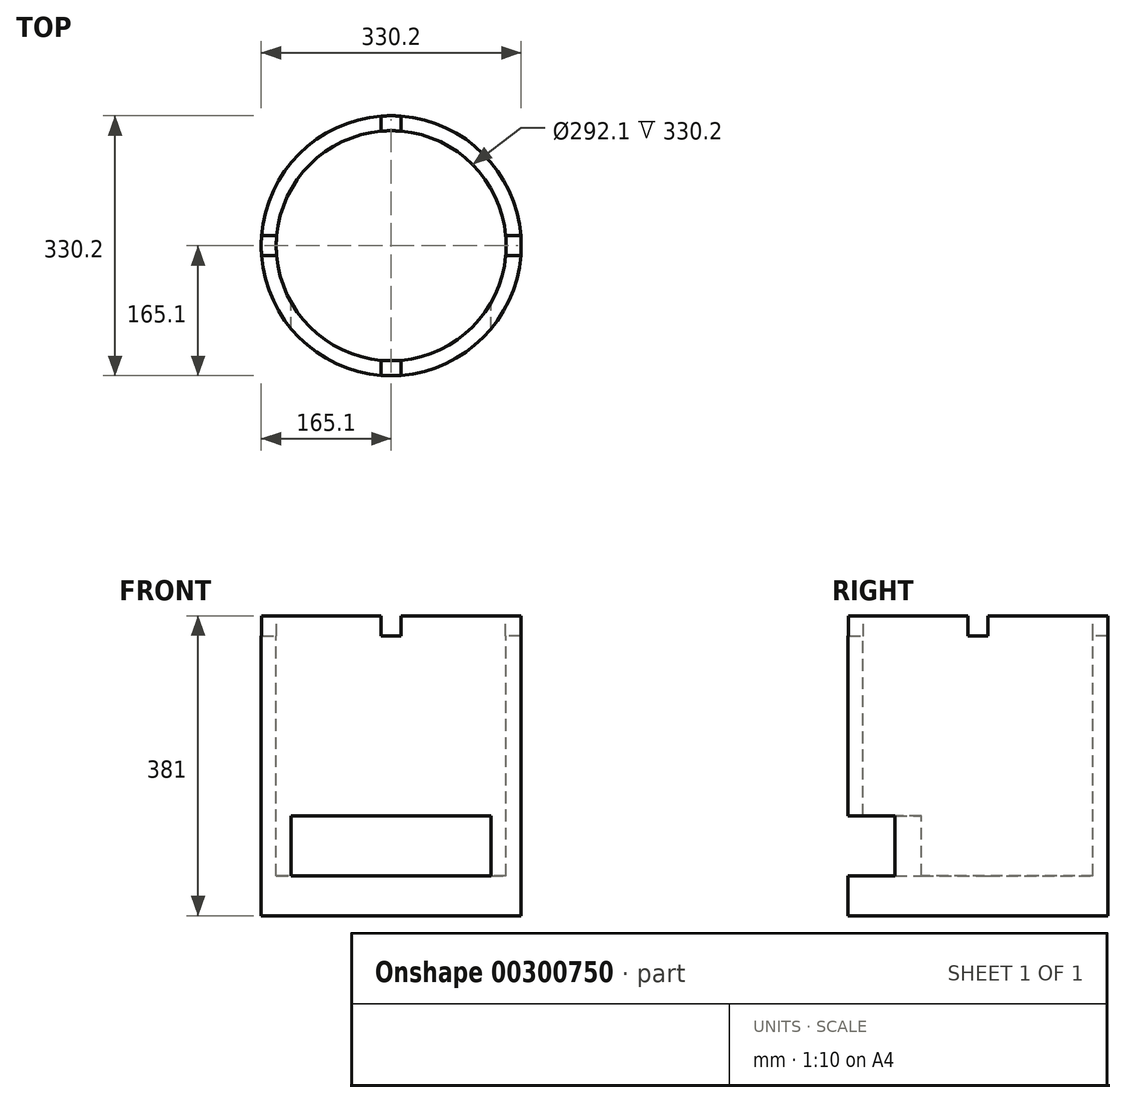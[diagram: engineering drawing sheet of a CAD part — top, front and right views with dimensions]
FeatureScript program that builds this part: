
annotation { "Feature Type Name" : "Feature", "Feature Type Description" : "" }
export const myFeature = defineFeature(function(context is Context, id is Id, definition is map)
    precondition{}
    {
        {
            var Q0;
            Q0=qCreatedBy(makeId("Top.planeOp"),FACE);
            var sketch = newSketch(context, id + "F0", { "sketchPlane" : qUnion([Q0])});
            skCircle(sketch, "E0", {"center": v(0, 0) * mm, "radius": 165.1 * mm});
            skSolve(sketch);
        }
        {
            var Q0;
            Q0=makeQuery(id+"F0.imprint","IMPRINT",FACE,{"disambiguationData":[TD([[makeQuery(id+"F0.imprint","IMPRINT",EDGE,{"derivedFrom":sQuery(id+"F0.wireOp",EDGE,"E0")}),1.0]])]});
            extrude(context, id + "F1", {"entities" : qUnion([Q0]), "depth" : 381 * mm});
        }
        {
            var Q0;
            Q0=makeQuery(id+"F1.opExtrude","CAP_FACE",FACE,{"disambiguationData":[OSD([sQuery(id+"F0.wireOp",EDGE,"E0")])],"isStart":false});
            var sketch = newSketch(context, id + "F2", { "sketchPlane" : qUnion([Q0])});
            skPoint(sketch, "E1.0", {"position": v(0, 0) * mm});
            skCircle(sketch, "E2", {"center": v(0, 0) * mm, "radius": 146.05 * mm});
            skSolve(sketch);
        }
        {
            var Q0;
            Q0=makeQuery(id+"F2.imprint","IMPRINT",FACE,{"disambiguationData":[TD([[makeQuery(id+"F2.imprint","IMPRINT",EDGE,{"derivedFrom":sQuery(id+"F2.wireOp",EDGE,"E2")}),1.0]])]});
            extrude(context, id + "F3", {"entities" : qUnion([Q0]), "operationType" : NewBodyOperationType.REMOVE, "oppositeDirection" : true, "depth" : 330.2 * mm});
        }
        {
            var Q0;
            Q0=qCreatedBy(makeId("Front.planeOp"),FACE);
            var sketch = newSketch(context, id + "F4", { "sketchPlane" : qUnion([Q0])});
            skLineSegment(sketch, "E3", {"start": v(-165.1, 0) * mm, "end": v(-165.1, 381) * mm});
            skLineSegment(sketch, "E4", {"start": v(165.1, 381) * mm, "end": v(165.1, 0) * mm});
            skLineSegment(sketch, "E5", {"start": v(165.1, 381) * mm, "end": v(-165.1, 381) * mm});
            skLineSegment(sketch, "E6", {"start": v(165.1, 0) * mm, "end": v(-165.1, 0) * mm});
            skPoint(sketch, "E7", {"position": v(0, 0) * mm});
            skLineSegment(sketch, "E8", {"start": v(0, 381) * mm, "end": v(0, 0) * mm, "construction": true});
            skLineSegment(sketch, "E9.bottom", {"start": v(127, 127) * mm, "end": v(-127, 127) * mm});
            skLineSegment(sketch, "E9.top", {"start": v(127, 50.8) * mm, "end": v(-127, 50.8) * mm});
            skLineSegment(sketch, "E9.left", {"start": v(127, 127) * mm, "end": v(127, 50.8) * mm});
            skLineSegment(sketch, "E9.right", {"start": v(-127, 127) * mm, "end": v(-127, 50.8) * mm});
            skPoint(sketch, "E10", {"position": v(-514.73, 96.28) * mm});
            skSolve(sketch);
        }
        {
            var Q0;
            Q0=makeQuery(id+"F4.imprint","IMPRINT",FACE,{"disambiguationData":[TD([[makeQuery(id+"F4.imprint","IMPRINT",EDGE,{"derivedFrom":sQuery(id+"F4.wireOp",EDGE,"E9.bottom")}),1.0]])]});
            extrude(context, id + "F5", {"entities" : qUnion([Q0]), "operationType" : NewBodyOperationType.REMOVE, "depth" : 177.8 * mm});
        }
        {
            var Q0;
            Q0=makeQuery(id+"F1.opExtrude","CAP_FACE",FACE,{"disambiguationData":[OSD([sQuery(id+"F0.wireOp",EDGE,"E0")])],"isStart":false});
            var sketch = newSketch(context, id + "F6", { "sketchPlane" : qUnion([Q0])});
            skCircle(sketch, "E11.0.0", {"center": v(0, 0) * mm, "radius": 165.1 * mm, "construction": true});
            skCircle(sketch, "E12.0", {"center": v(0, 0) * mm, "radius": 146.05 * mm, "construction": true});
            skLineSegment(sketch, "E13", {"start": v(-165.1, 0) * mm, "end": v(165.1, 0) * mm, "construction": true});
            skLineSegment(sketch, "E14", {"start": v(0, 165.1) * mm, "end": v(0, -165.1) * mm, "construction": true});
            skLineSegment(sketch, "E15.bottom", {"start": v(-12.7, 165.1) * mm, "end": v(12.7, 165.1) * mm});
            skLineSegment(sketch, "E15.top", {"start": v(-12.7, 145.5) * mm, "end": v(12.7, 145.5) * mm});
            skLineSegment(sketch, "E15.left", {"start": v(-12.7, 165.1) * mm, "end": v(-12.7, 145.5) * mm});
            skLineSegment(sketch, "E15.right", {"start": v(12.7, 165.1) * mm, "end": v(12.7, 145.5) * mm});
            skLineSegment(sketch, "E16.bottom", {"start": v(-165.1, -12.7) * mm, "end": v(-145.5, -12.7) * mm});
            skLineSegment(sketch, "E16.top", {"start": v(-165.1, 12.7) * mm, "end": v(-145.5, 12.7) * mm});
            skLineSegment(sketch, "E16.left", {"start": v(-165.1, -12.7) * mm, "end": v(-165.1, 12.7) * mm});
            skLineSegment(sketch, "E16.right", {"start": v(-145.5, -12.7) * mm, "end": v(-145.5, 12.7) * mm});
            skLineSegment(sketch, "E17.bottom", {"start": v(165.1, 12.7) * mm, "end": v(145.5, 12.7) * mm});
            skLineSegment(sketch, "E17.top", {"start": v(165.1, -12.7) * mm, "end": v(145.5, -12.7) * mm});
            skLineSegment(sketch, "E17.left", {"start": v(165.1, 12.7) * mm, "end": v(165.1, -12.7) * mm});
            skLineSegment(sketch, "E17.right", {"start": v(145.5, 12.7) * mm, "end": v(145.5, -12.7) * mm});
            skLineSegment(sketch, "E18.bottom", {"start": v(12.7, -165.1) * mm, "end": v(-12.7, -165.1) * mm});
            skLineSegment(sketch, "E18.top", {"start": v(12.7, -145.5) * mm, "end": v(-12.7, -145.5) * mm});
            skLineSegment(sketch, "E18.left", {"start": v(12.7, -165.1) * mm, "end": v(12.7, -145.5) * mm});
            skLineSegment(sketch, "E18.right", {"start": v(-12.7, -165.1) * mm, "end": v(-12.7, -145.5) * mm});
            skSolve(sketch);
        }
        {
            var Q0;
            {var subQ0=makeQuery(id+"F1.opExtrude","CAP_EDGE",EDGE,{"disambiguationData":[OSD([sQuery(id+"F0.wireOp",EDGE,"E0")])],"isStart":false});var subQ1=makeQuery(id+"F6.imprint","INTERSECT",VERTEX,{"derivedFrom":[subQ0,sQuery(id+"F6.wireOp",EDGE,"E15.bottom")]});Q0=makeQuery(id+"F6.imprint","IMPRINT",FACE,{"disambiguationData":[TD([[makeQuery(id+"F6.imprint","IMPRINT",EDGE,{"disambiguationData":[TD([[subQ1,-1.0]])],"derivedFrom":subQ0}),1.0]])]});}
            var Q1;
            {var subQ0=sQuery(id+"F6.wireOp",EDGE,"E16.bottom");var subQ1=makeQuery(id+"F1.opExtrude","CAP_EDGE",EDGE,{"disambiguationData":[OSD([sQuery(id+"F0.wireOp",EDGE,"E0")])],"isStart":false});var subQ2=makeQuery(id+"F6.imprint","INTERSECT",VERTEX,{"derivedFrom":[subQ1,subQ0]});Q1=makeQuery(id+"F6.imprint","IMPRINT",FACE,{"disambiguationData":[TD([[makeQuery(id+"F6.imprint","IMPRINT",EDGE,{"disambiguationData":[TD([[subQ2,1.0]])],"derivedFrom":subQ1}),1.0]])]});}
            var Q2;
            {var subQ0=makeQuery(id+"F1.opExtrude","CAP_EDGE",EDGE,{"disambiguationData":[OSD([sQuery(id+"F0.wireOp",EDGE,"E0")])],"isStart":false});var subQ1=makeQuery(id+"F6.imprint","INTERSECT",VERTEX,{"derivedFrom":[subQ0,sQuery(id+"F6.wireOp",EDGE,"E18.bottom")]});Q2=makeQuery(id+"F6.imprint","IMPRINT",FACE,{"disambiguationData":[TD([[makeQuery(id+"F6.imprint","IMPRINT",EDGE,{"disambiguationData":[TD([[subQ1,-1.0]])],"derivedFrom":subQ0}),1.0]])]});}
            var Q3;
            {var subQ0=sQuery(id+"F6.wireOp",EDGE,"E17.bottom");var subQ1=makeQuery(id+"F1.opExtrude","CAP_EDGE",EDGE,{"disambiguationData":[OSD([sQuery(id+"F0.wireOp",EDGE,"E0")])],"isStart":false});var subQ2=makeQuery(id+"F6.imprint","INTERSECT",VERTEX,{"derivedFrom":[subQ1,subQ0]});Q3=makeQuery(id+"F6.imprint","IMPRINT",FACE,{"disambiguationData":[TD([[makeQuery(id+"F6.imprint","IMPRINT",EDGE,{"disambiguationData":[TD([[subQ2,1.0]])],"derivedFrom":subQ1}),1.0]])]});}
            extrude(context, id + "F7", {"entities" : qUnion([Q0, Q1, Q2, Q3]), "operationType" : NewBodyOperationType.REMOVE, "oppositeDirection" : true, "depth" : 25.4 * mm});
        }
    });
